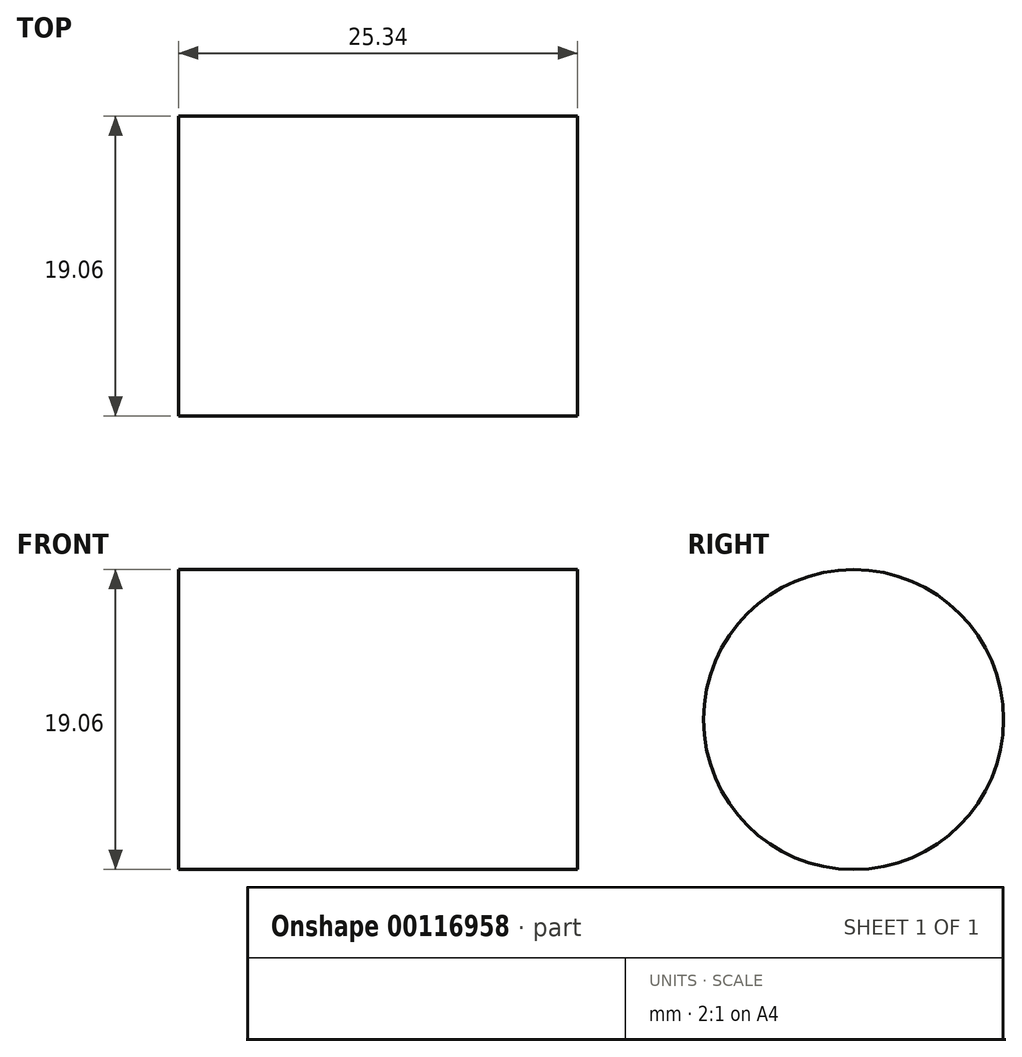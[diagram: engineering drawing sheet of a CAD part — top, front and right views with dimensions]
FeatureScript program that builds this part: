
annotation { "Feature Type Name" : "Feature", "Feature Type Description" : "" }
export const myFeature = defineFeature(function(context is Context, id is Id, definition is map)
    precondition{}
    {
        {
            var Q0;
            Q0=qCreatedBy(makeId("Right.planeOp"),FACE);
            var sketch = newSketch(context, id + "F0", { "sketchPlane" : qUnion([Q0])});
            skCircle(sketch, "E0", {"center": v(0, 0) * mm, "radius": 9.53 * mm});
            skSolve(sketch);
        }
        {
            var Q0;
            Q0=makeQuery(id+"F0.imprint","IMPRINT",FACE,{"disambiguationData":[TD([[makeQuery(id+"F0.imprint","IMPRINT",EDGE,{"derivedFrom":sQuery(id+"F0.wireOp",EDGE,"E0")}),1.0]])]});
            extrude(context, id + "F1", {"entities" : qUnion([Q0]), "endBound" : BoundingType.SYMMETRIC, "depth" : 25.35 * mm});
        }
    });
